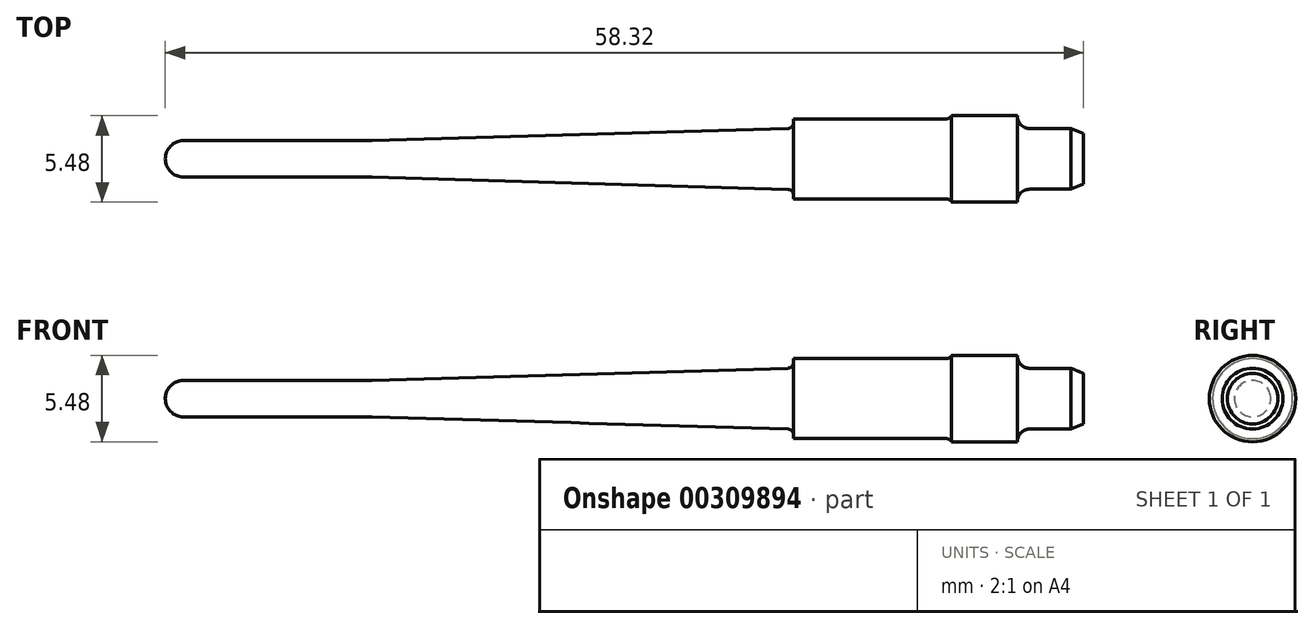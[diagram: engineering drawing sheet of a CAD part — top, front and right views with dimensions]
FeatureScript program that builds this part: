
annotation { "Feature Type Name" : "Feature", "Feature Type Description" : "" }
export const myFeature = defineFeature(function(context is Context, id is Id, definition is map)
    precondition{}
    {
        {
            var Q0;
            Q0=qCreatedBy(makeId("Front.planeOp"),FACE);
            var sketch = newSketch(context, id + "F0", { "sketchPlane" : qUnion([Q0])});
            skLineSegment(sketch, "E0", {"start": v(0, 0) * mm, "end": v(0, 1.93) * mm});
            skLineSegment(sketch, "E1", {"start": v(0, 1.93) * mm, "end": v(-4.2, 1.93) * mm});
            skLineSegment(sketch, "E2", {"start": v(-4.2, 1.93) * mm, "end": v(-4.2, 2.74) * mm});
            skLineSegment(sketch, "E3", {"start": v(-4.2, 2.74) * mm, "end": v(-8.38, 2.74) * mm});
            skLineSegment(sketch, "E4", {"start": v(-8.38, 2.74) * mm, "end": v(-8.38, 2.54) * mm});
            skLineSegment(sketch, "E5", {"start": v(-8.38, 2.54) * mm, "end": v(-18.41, 2.54) * mm});
            skLineSegment(sketch, "E6", {"start": v(-18.41, 2.54) * mm, "end": v(-18.41, 1.94) * mm});
            skLineSegment(sketch, "E7", {"start": v(-58.32, 0) * mm, "end": v(0, 0) * mm});
            skLineSegment(sketch, "E8", {"start": v(-18.41, 1.94) * mm, "end": v(-45.24, 1.16) * mm});
            skLineSegment(sketch, "E9", {"start": v(-45.24, 1.16) * mm, "end": v(-57.16, 1.16) * mm});
            skArc(sketch, "E10", {"start": v(-57.16, 1.16) * mm, "mid": v(-57.98, 0.82) * mm, "end": v(-58.32, 0) * mm});
            skPoint(sketch, "E11.orphan", {"position": v(-58.32, 1.16) * mm});
            skSolve(sketch);
        }
        {
            var Q0;
            Q0=makeQuery(id+"F0.imprint","IMPRINT",FACE,{"disambiguationData":[TD([[makeQuery(id+"F0.imprint","IMPRINT",EDGE,{"derivedFrom":sQuery(id+"F0.wireOp",EDGE,"E0")}),1.0]])]});
            var Q1;
            Q1=sQuery(id+"F0.wireOp",EDGE,"E7");
            revolve(context, id + "F1", {"entities" : qUnion([Q0]), "axis" : qUnion([Q1]), "revolveType" : RevolveType.FULL});
        }
        {
            var Q0;
            Q0=makeQuery(id+"F1.opRevolve","SWEPT_EDGE",EDGE,{"disambiguationData":[OSD([sQuery(id+"F0.wireOp",EDGE,"E8"),sQuery(id+"F0.wireOp",EDGE,"E9")])]});
            fillet(context, id + "F2", {"entities" : qUnion([Q0]), "radius" : 3.17 * mm, "tangentPropagation" : true, "allowEdgeOverflow" : false});
        }
        {
            var Q0;
            Q0=makeQuery(id+"F1.opRevolve","SWEPT_EDGE",EDGE,{"disambiguationData":[OSD([sQuery(id+"F0.wireOp",EDGE,"E6"),sQuery(id+"F0.wireOp",EDGE,"E8")])]});
            var Q1;
            Q1=makeQuery(id+"F1.opRevolve","SWEPT_EDGE",EDGE,{"disambiguationData":[OSD([sQuery(id+"F0.wireOp",EDGE,"E4"),sQuery(id+"F0.wireOp",EDGE,"E5")])]});
            fillet(context, id + "F3", {"entities" : qUnion([Q0, Q1]), "radius" : 0.38 * mm, "tangentPropagation" : true, "allowEdgeOverflow" : false});
        }
        {
            var Q0;
            Q0=makeQuery(id+"F1.opRevolve","SWEPT_EDGE",EDGE,{"disambiguationData":[OSD([sQuery(id+"F0.wireOp",EDGE,"E1"),sQuery(id+"F0.wireOp",EDGE,"E2")])]});
            fillet(context, id + "F4", {"entities" : qUnion([Q0]), "radius" : 0.76 * mm, "tangentPropagation" : true, "allowEdgeOverflow" : false});
        }
        {
            var Q0;
            Q0=makeQuery(id+"F1.opRevolve","SWEPT_EDGE",EDGE,{"disambiguationData":[OSD([sQuery(id+"F0.wireOp",EDGE,"E0"),sQuery(id+"F0.wireOp",EDGE,"E1")])]});
            chamfer(context, id + "F5", {"entities" : qUnion([Q0]), "chamferType" : ChamferType.OFFSET_ANGLE, "width" : 0.8 * mm, "oppositeDirection" : false, "angle" : 22.5 * degree, "tangentPropagation" : true});
        }
    });
